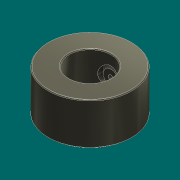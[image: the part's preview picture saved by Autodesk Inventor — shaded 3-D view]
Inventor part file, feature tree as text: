
AUTODESK INVENTOR PART (.ipt)
format: ipt  version: 2016 (Build 200138000, 138)  size: 154,624 bytes
history: native  units: mm
features: fillet x1, other x1
ambient origin geometry x8: Origin, YZ Plane, XZ Plane, XY Plane, X Axis, Y Axis, Z Axis, Center Point
bodies: Solid1 (feature_tree), Solid2 (feature_tree)
feature tree (2):
  fillet  "Fillet1"  [1 undecoded]
  other  "Cut-Extrude2"
note: 1 required parameter value undecoded (feature->parameter linkage not recoverable at this tier; creation-order binding heuristic only, values carry confidence <= 0.55)
